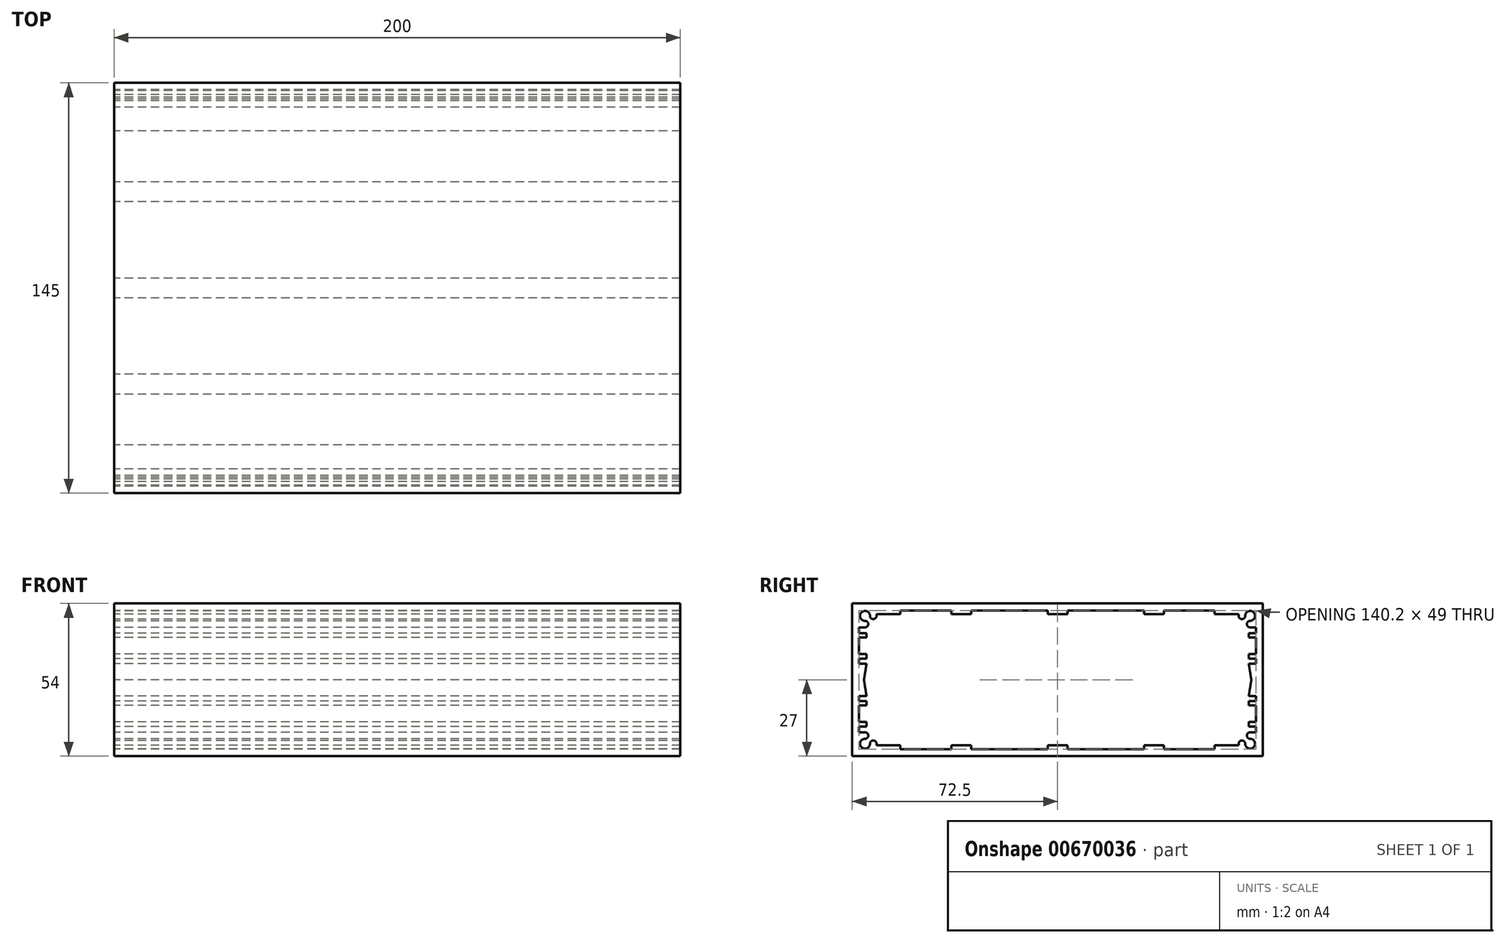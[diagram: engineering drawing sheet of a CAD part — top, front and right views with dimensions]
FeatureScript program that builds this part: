
annotation { "Feature Type Name" : "Feature", "Feature Type Description" : "" }
export const myFeature = defineFeature(function(context is Context, id is Id, definition is map)
    precondition{}
    {
        {
            var Q0;
            Q0=qCreatedBy(makeId("Right.planeOp"),FACE);
            var sketch = newSketch(context, id + "F0", { "sketchPlane" : qUnion([Q0])});
            skLineSegment(sketch, "E0.bottom", {"start": v(0, 0) * mm, "end": v(145, 0) * mm});
            skLineSegment(sketch, "E0.top", {"start": v(0, 54) * mm, "end": v(145, 54) * mm});
            skLineSegment(sketch, "E0.left", {"start": v(0, 0) * mm, "end": v(0, 54) * mm});
            skLineSegment(sketch, "E0.right", {"start": v(145, 0) * mm, "end": v(145, 54) * mm});
            skLineSegment(sketch, "E1", {"start": v(72.5, 54) * mm, "end": v(72.5, 0) * mm, "construction": true});
            skLineSegment(sketch, "E2", {"start": v(0, 27) * mm, "end": v(145, 27) * mm, "construction": true});
            skPoint(sketch, "E3.middle", {"position": v(72.5, 27) * mm});
            skLineSegment(sketch, "E4", {"start": v(72.5, 50.2) * mm, "end": v(69, 50.2) * mm});
            skLineSegment(sketch, "E5", {"start": v(69, 50.2) * mm, "end": v(69, 51.5) * mm});
            skLineSegment(sketch, "E6", {"start": v(69, 51.5) * mm, "end": v(42, 51.5) * mm});
            skLineSegment(sketch, "E7", {"start": v(42, 51.5) * mm, "end": v(42, 50.2) * mm});
            skLineSegment(sketch, "E8", {"start": v(42, 50.2) * mm, "end": v(35, 50.2) * mm});
            skLineSegment(sketch, "E9", {"start": v(35, 50.2) * mm, "end": v(35, 51.5) * mm});
            skLineSegment(sketch, "E10", {"start": v(35, 51.5) * mm, "end": v(17, 51.5) * mm});
            skLineSegment(sketch, "E11", {"start": v(17, 51.5) * mm, "end": v(17, 50.2) * mm});
            skLineSegment(sketch, "E12", {"start": v(17, 50.2) * mm, "end": v(8.55, 50.2) * mm});
            skArc(sketch, "E13", {"start": v(6.25, 49.6) * mm, "mid": v(3.26, 50.84) * mm, "end": v(4.5, 47.85) * mm});
            skArc(sketch, "E14", {"start": v(6.25, 49.6) * mm, "mid": v(7.4, 48.45) * mm, "end": v(8.55, 49.6) * mm});
            skLineSegment(sketch, "E15", {"start": v(8.55, 49.6) * mm, "end": v(8.55, 50.2) * mm});
            skArc(sketch, "E16", {"start": v(4.5, 45.55) * mm, "mid": v(5.65, 46.7) * mm, "end": v(4.5, 47.85) * mm});
            skLineSegment(sketch, "E17", {"start": v(4.5, 45.55) * mm, "end": v(2.4, 45.55) * mm});
            skLineSegment(sketch, "E18", {"start": v(2.4, 45.55) * mm, "end": v(2.4, 43.5) * mm});
            skLineSegment(sketch, "E19", {"start": v(2.4, 43.5) * mm, "end": v(5, 43.5) * mm});
            skLineSegment(sketch, "E20", {"start": v(5, 43.5) * mm, "end": v(5, 41.9) * mm});
            skLineSegment(sketch, "E21", {"start": v(5, 41.9) * mm, "end": v(2.4, 41.9) * mm});
            skLineSegment(sketch, "E22", {"start": v(2.4, 41.9) * mm, "end": v(2.4, 36.1) * mm});
            skLineSegment(sketch, "E23", {"start": v(2.4, 36.1) * mm, "end": v(5, 36.1) * mm});
            skLineSegment(sketch, "E24", {"start": v(5, 36.1) * mm, "end": v(5, 34.5) * mm});
            skLineSegment(sketch, "E25", {"start": v(5, 34.5) * mm, "end": v(2.4, 34.5) * mm});
            skLineSegment(sketch, "E26", {"start": v(2.4, 34.5) * mm, "end": v(2.4, 32.68) * mm});
            skLineSegment(sketch, "E27", {"start": v(2.4, 32.68) * mm, "end": v(5, 32.68) * mm});
            skLineSegment(sketch, "E28", {"start": v(5, 32.68) * mm, "end": v(4.1, 27) * mm});
            skLineSegment(sketch, "E29.MirrorCS", {"start": v(103, 51.5) * mm, "end": v(103, 50.2) * mm});
            skLineSegment(sketch, "E30.MirrorCS", {"start": v(142.6, 32.68) * mm, "end": v(140, 32.68) * mm});
            skLineSegment(sketch, "E31.MirrorCS", {"start": v(110, 50.2) * mm, "end": v(110, 51.5) * mm});
            skLineSegment(sketch, "E32.MirrorCS", {"start": v(140, 41.9) * mm, "end": v(142.6, 41.9) * mm});
            skLineSegment(sketch, "E33.MirrorCS", {"start": v(128, 51.5) * mm, "end": v(128, 50.2) * mm});
            skLineSegment(sketch, "E34.MirrorCS", {"start": v(140, 34.5) * mm, "end": v(142.6, 34.5) * mm});
            skLineSegment(sketch, "E35.MirrorCS", {"start": v(140, 36.1) * mm, "end": v(140, 34.5) * mm});
            skLineSegment(sketch, "E36.MirrorCS", {"start": v(76, 50.2) * mm, "end": v(76, 51.5) * mm});
            skLineSegment(sketch, "E37.MirrorCS", {"start": v(136.45, 49.6) * mm, "end": v(136.45, 50.2) * mm});
            skLineSegment(sketch, "E38.MirrorCS", {"start": v(142.6, 45.55) * mm, "end": v(142.6, 43.5) * mm});
            skLineSegment(sketch, "E39.MirrorCS", {"start": v(142.6, 43.5) * mm, "end": v(140, 43.5) * mm});
            skLineSegment(sketch, "E40.MirrorCS", {"start": v(140.5, 45.55) * mm, "end": v(142.6, 45.55) * mm});
            skLineSegment(sketch, "E41.MirrorCS", {"start": v(140, 43.5) * mm, "end": v(140, 41.9) * mm});
            skLineSegment(sketch, "E42.MirrorCS", {"start": v(142.6, 34.5) * mm, "end": v(142.6, 32.68) * mm});
            skArc(sketch, "E43.MirrorCS", {"start": v(138.75, 49.6) * mm, "mid": v(137.6, 48.45) * mm, "end": v(136.45, 49.6) * mm});
            skLineSegment(sketch, "E44.MirrorCS", {"start": v(142.6, 36.1) * mm, "end": v(140, 36.1) * mm});
            skLineSegment(sketch, "E45.MirrorCS", {"start": v(142.6, 41.9) * mm, "end": v(142.6, 36.1) * mm});
            skLineSegment(sketch, "E46.MirrorCS", {"start": v(110, 51.5) * mm, "end": v(128, 51.5) * mm});
            skLineSegment(sketch, "E47.MirrorCS", {"start": v(140, 32.68) * mm, "end": v(140.9, 27) * mm});
            skLineSegment(sketch, "E48.MirrorCS", {"start": v(128, 50.2) * mm, "end": v(136.45, 50.2) * mm});
            skLineSegment(sketch, "E49.MirrorCS", {"start": v(76, 51.5) * mm, "end": v(103, 51.5) * mm});
            skLineSegment(sketch, "E50.MirrorCS", {"start": v(72.5, 50.2) * mm, "end": v(76, 50.2) * mm});
            skLineSegment(sketch, "E51.MirrorCS", {"start": v(103, 50.2) * mm, "end": v(110, 50.2) * mm});
            skArc(sketch, "E52.MirrorCS", {"start": v(138.75, 49.6) * mm, "mid": v(141.74, 50.84) * mm, "end": v(140.5, 47.85) * mm});
            skArc(sketch, "E53.MirrorCS", {"start": v(140.5, 45.55) * mm, "mid": v(139.35, 46.7) * mm, "end": v(140.5, 47.85) * mm});
            skLineSegment(sketch, "E54.MirrorCS", {"start": v(2.4, 10.5) * mm, "end": v(5, 10.5) * mm});
            skLineSegment(sketch, "E55.MirrorCS", {"start": v(2.4, 8.45) * mm, "end": v(2.4, 10.5) * mm});
            skLineSegment(sketch, "E56.MirrorCS", {"start": v(4.5, 8.45) * mm, "end": v(2.4, 8.45) * mm});
            skLineSegment(sketch, "E57.MirrorCS", {"start": v(5, 12.1) * mm, "end": v(2.4, 12.1) * mm});
            skLineSegment(sketch, "E58.MirrorCS", {"start": v(5, 10.5) * mm, "end": v(5, 12.1) * mm});
            skArc(sketch, "E59.MirrorCS", {"start": v(138.75, 4.4) * mm, "mid": v(137.6, 5.55) * mm, "end": v(136.45, 4.4) * mm});
            skLineSegment(sketch, "E60.MirrorCS", {"start": v(8.55, 4.4) * mm, "end": v(8.55, 3.8) * mm});
            skLineSegment(sketch, "E61.MirrorCS", {"start": v(136.45, 4.4) * mm, "end": v(136.45, 3.8) * mm});
            skLineSegment(sketch, "E62.MirrorCS", {"start": v(72.5, 3.8) * mm, "end": v(69, 3.8) * mm});
            skArc(sketch, "E63.MirrorCS", {"start": v(6.25, 4.4) * mm, "mid": v(7.4, 5.55) * mm, "end": v(8.55, 4.4) * mm});
            skLineSegment(sketch, "E64.MirrorCS", {"start": v(69, 3.8) * mm, "end": v(69, 2.5) * mm});
            skLineSegment(sketch, "E65.MirrorCS", {"start": v(142.6, 17.9) * mm, "end": v(140, 17.9) * mm});
            skLineSegment(sketch, "E66.MirrorCS", {"start": v(5, 19.5) * mm, "end": v(2.4, 19.5) * mm});
            skLineSegment(sketch, "E67.MirrorCS", {"start": v(140, 12.1) * mm, "end": v(142.6, 12.1) * mm});
            skArc(sketch, "E68.MirrorCS", {"start": v(4.5, 8.45) * mm, "mid": v(5.65, 7.3) * mm, "end": v(4.5, 6.15) * mm});
            skLineSegment(sketch, "E69.MirrorCS", {"start": v(140, 17.9) * mm, "end": v(140, 19.5) * mm});
            skLineSegment(sketch, "E70.MirrorCS", {"start": v(2.4, 21.32) * mm, "end": v(5, 21.32) * mm});
            skLineSegment(sketch, "E71.MirrorCS", {"start": v(5, 17.9) * mm, "end": v(5, 19.5) * mm});
            skLineSegment(sketch, "E72.MirrorCS", {"start": v(140.5, 8.45) * mm, "end": v(142.6, 8.45) * mm});
            skLineSegment(sketch, "E73.MirrorCS", {"start": v(140, 19.5) * mm, "end": v(142.6, 19.5) * mm});
            skLineSegment(sketch, "E74.MirrorCS", {"start": v(72.5, 3.8) * mm, "end": v(76, 3.8) * mm});
            skLineSegment(sketch, "E75.MirrorCS", {"start": v(2.4, 12.1) * mm, "end": v(2.4, 17.9) * mm});
            skLineSegment(sketch, "E76.MirrorCS", {"start": v(142.6, 8.45) * mm, "end": v(142.6, 10.5) * mm});
            skLineSegment(sketch, "E77.MirrorCS", {"start": v(2.4, 17.9) * mm, "end": v(5, 17.9) * mm});
            skLineSegment(sketch, "E78.MirrorCS", {"start": v(142.6, 10.5) * mm, "end": v(140, 10.5) * mm});
            skLineSegment(sketch, "E79.MirrorCS", {"start": v(128, 2.5) * mm, "end": v(128, 3.8) * mm});
            skLineSegment(sketch, "E80.MirrorCS", {"start": v(2.4, 19.5) * mm, "end": v(2.4, 21.32) * mm});
            skLineSegment(sketch, "E81.MirrorCS", {"start": v(103, 2.5) * mm, "end": v(103, 3.8) * mm});
            skLineSegment(sketch, "E82.MirrorCS", {"start": v(42, 2.5) * mm, "end": v(42, 3.8) * mm});
            skLineSegment(sketch, "E83.MirrorCS", {"start": v(142.6, 21.32) * mm, "end": v(140, 21.32) * mm});
            skLineSegment(sketch, "E84.MirrorCS", {"start": v(76, 3.8) * mm, "end": v(76, 2.5) * mm});
            skLineSegment(sketch, "E85.MirrorCS", {"start": v(140, 10.5) * mm, "end": v(140, 12.1) * mm});
            skLineSegment(sketch, "E86.MirrorCS", {"start": v(17, 2.5) * mm, "end": v(17, 3.8) * mm});
            skLineSegment(sketch, "E87.MirrorCS", {"start": v(110, 3.8) * mm, "end": v(110, 2.5) * mm});
            skLineSegment(sketch, "E88.MirrorCS", {"start": v(142.6, 19.5) * mm, "end": v(142.6, 21.32) * mm});
            skLineSegment(sketch, "E89.MirrorCS", {"start": v(142.6, 12.1) * mm, "end": v(142.6, 17.9) * mm});
            skArc(sketch, "E90.MirrorCS", {"start": v(140.5, 8.45) * mm, "mid": v(139.35, 7.3) * mm, "end": v(140.5, 6.15) * mm});
            skLineSegment(sketch, "E91.MirrorCS", {"start": v(35, 3.8) * mm, "end": v(35, 2.5) * mm});
            skArc(sketch, "E92.MirrorCS", {"start": v(6.25, 4.4) * mm, "mid": v(3.26, 3.16) * mm, "end": v(4.5, 6.15) * mm});
            skArc(sketch, "E93.MirrorCS", {"start": v(138.75, 4.4) * mm, "mid": v(141.74, 3.16) * mm, "end": v(140.5, 6.15) * mm});
            skLineSegment(sketch, "E94.MirrorCS", {"start": v(5, 21.32) * mm, "end": v(4.1, 27) * mm});
            skLineSegment(sketch, "E95.MirrorCS", {"start": v(140, 21.32) * mm, "end": v(140.9, 27) * mm});
            skLineSegment(sketch, "E96.MirrorCS", {"start": v(17, 3.8) * mm, "end": v(8.55, 3.8) * mm});
            skLineSegment(sketch, "E97.MirrorCS", {"start": v(128, 3.8) * mm, "end": v(136.45, 3.8) * mm});
            skLineSegment(sketch, "E98.MirrorCS", {"start": v(103, 3.8) * mm, "end": v(110, 3.8) * mm});
            skLineSegment(sketch, "E99.MirrorCS", {"start": v(76, 2.5) * mm, "end": v(103, 2.5) * mm});
            skLineSegment(sketch, "E100.MirrorCS", {"start": v(42, 3.8) * mm, "end": v(35, 3.8) * mm});
            skLineSegment(sketch, "E101.MirrorCS", {"start": v(35, 2.5) * mm, "end": v(17, 2.5) * mm});
            skLineSegment(sketch, "E102.MirrorCS", {"start": v(110, 2.5) * mm, "end": v(128, 2.5) * mm});
            skLineSegment(sketch, "E103.MirrorCS", {"start": v(69, 2.5) * mm, "end": v(42, 2.5) * mm});
            skSolve(sketch);
        }
        {
            var Q0;
            Q0 = qSketchRegion(id + "F0", true);
            extrude(context, id + "F1", {"entities" : qUnion([Q0]), "depth" : 200 * mm, "offsetDistance" : 25 * mm});
        }
    });
